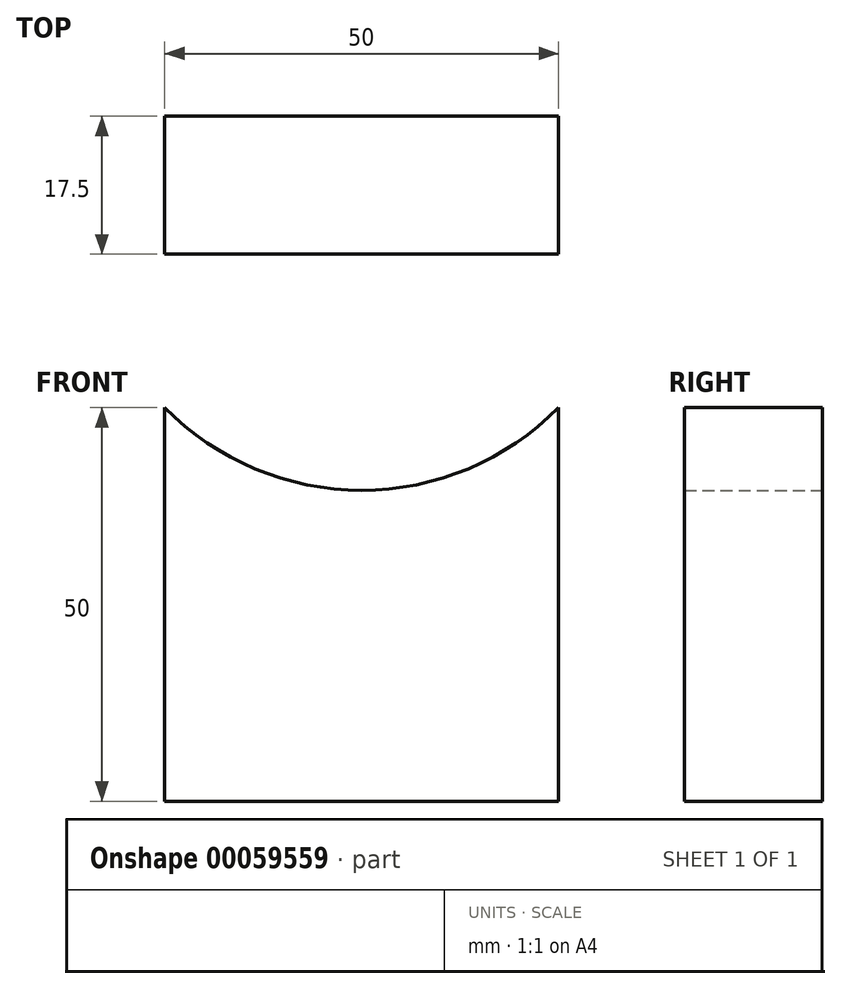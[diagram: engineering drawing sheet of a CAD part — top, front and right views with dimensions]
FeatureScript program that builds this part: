
annotation { "Feature Type Name" : "Feature", "Feature Type Description" : "" }
export const myFeature = defineFeature(function(context is Context, id is Id, definition is map)
    precondition{}
    {
        {
            var Q0;
            Q0=qCreatedBy(makeId("Front.planeOp"),FACE);
            var sketch = newSketch(context, id + "F0", { "sketchPlane" : qUnion([Q0])});
            skLineSegment(sketch, "E0", {"start": v(-25, -33.47) * mm, "end": v(25, -33.47) * mm});
            skLineSegment(sketch, "E1", {"start": v(25, -33.47) * mm, "end": v(25, 16.53) * mm});
            skLineSegment(sketch, "E2", {"start": v(-25, -33.47) * mm, "end": v(-25, 16.53) * mm});
            skLineSegment(sketch, "E3", {"start": v(0, -33.47) * mm, "end": v(0, 51.4) * mm, "construction": true});
            skPoint(sketch, "E3.endSnap0", {"position": v(0, -33.47) * mm});
            skArc(sketch, "E4", {"start": v(-25, 16.53) * mm, "mid": v(0, 6.03) * mm, "end": v(25, 16.53) * mm});
            skSolve(sketch);
        }
        {
            var Q0;
            Q0=makeQuery(id+"F0.imprint","IMPRINT",FACE,{"disambiguationData":[TD([[makeQuery(id+"F0.imprint","IMPRINT",EDGE,{"derivedFrom":sQuery(id+"F0.wireOp",EDGE,"E0")}),1.0]])]});
            extrude(context, id + "F1", {"entities" : qUnion([Q0]), "depth" : 17.5 * mm});
        }
    });
